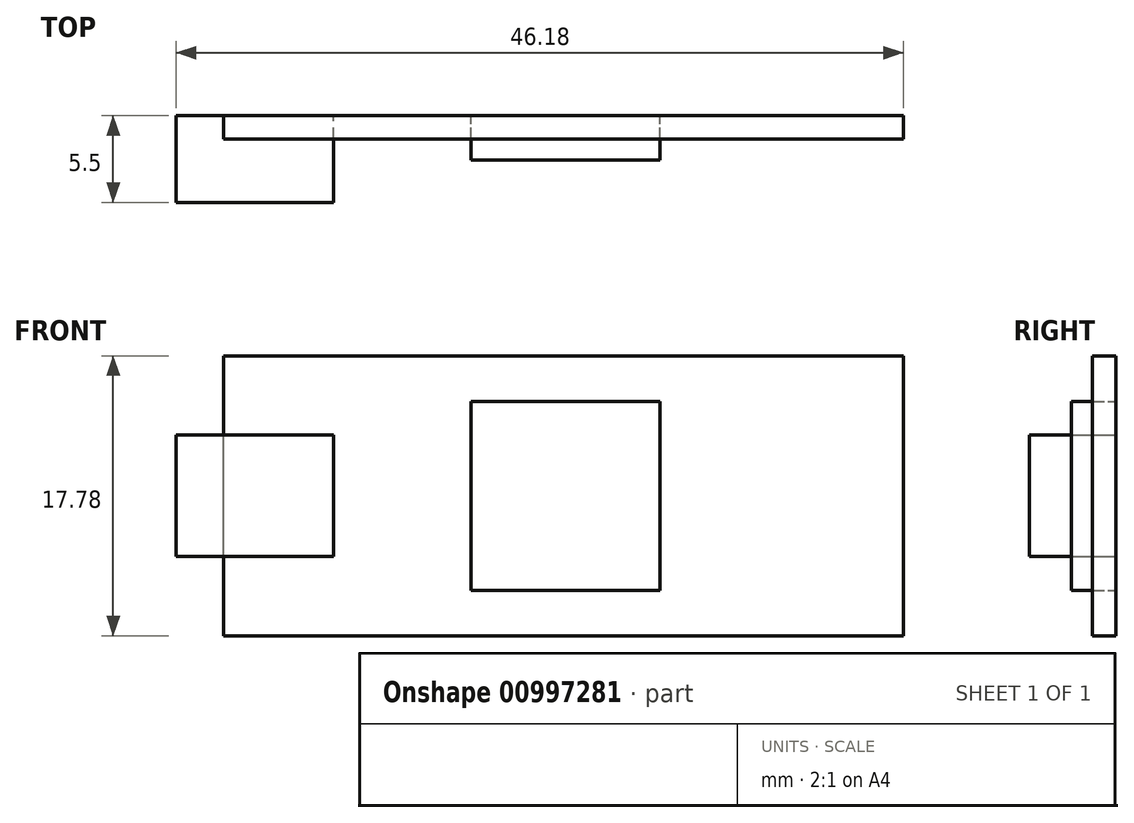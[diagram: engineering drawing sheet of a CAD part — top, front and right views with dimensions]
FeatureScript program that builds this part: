
annotation { "Feature Type Name" : "Feature", "Feature Type Description" : "" }
export const myFeature = defineFeature(function(context is Context, id is Id, definition is map)
    precondition{}
    {
        {
            var Q0;
            Q0=qCreatedBy(makeId("Front.planeOp"),FACE);
            var sketch = newSketch(context, id + "F0", { "sketchPlane" : qUnion([Q0])});
            skLineSegment(sketch, "E0.bottom", {"start": v(-43.18, 25.32) * mm, "end": v(0, 25.32) * mm});
            skLineSegment(sketch, "E0.top", {"start": v(-43.18, 43.1) * mm, "end": v(0, 43.1) * mm});
            skLineSegment(sketch, "E0.left", {"start": v(-43.18, 25.32) * mm, "end": v(-43.18, 43.1) * mm});
            skLineSegment(sketch, "E0.right", {"start": v(0, 25.32) * mm, "end": v(0, 43.1) * mm});
            skSolve(sketch);
        }
        {
            var Q0;
            Q0=qCreatedBy(makeId("Front.planeOp"),FACE);
            var sketch = newSketch(context, id + "F1", { "sketchPlane" : qUnion([Q0])});
            skLineSegment(sketch, "E1.bottom", {"start": v(-27.45, 28.21) * mm, "end": v(-15.45, 28.21) * mm});
            skLineSegment(sketch, "E1.top", {"start": v(-27.45, 40.21) * mm, "end": v(-15.45, 40.21) * mm});
            skLineSegment(sketch, "E1.left", {"start": v(-27.45, 28.21) * mm, "end": v(-27.45, 40.21) * mm});
            skLineSegment(sketch, "E1.right", {"start": v(-15.45, 28.21) * mm, "end": v(-15.45, 40.21) * mm});
            skPoint(sketch, "E2", {"position": v(-27.45, 34.21) * mm});
            skSolve(sketch);
        }
        {
            var Q0;
            Q0=qCreatedBy(makeId("Front.planeOp"),FACE);
            var sketch = newSketch(context, id + "F2", { "sketchPlane" : qUnion([Q0])});
            skLineSegment(sketch, "E3.bottom", {"start": v(-46.18, 38.06) * mm, "end": v(-36.18, 38.06) * mm});
            skLineSegment(sketch, "E3.top", {"start": v(-46.18, 30.36) * mm, "end": v(-36.18, 30.36) * mm});
            skLineSegment(sketch, "E3.left", {"start": v(-46.18, 38.06) * mm, "end": v(-46.18, 30.36) * mm});
            skLineSegment(sketch, "E3.right", {"start": v(-36.18, 38.06) * mm, "end": v(-36.18, 30.36) * mm});
            skPoint(sketch, "E4", {"position": v(-46.18, 34.21) * mm});
            skSolve(sketch);
        }
        {
            var Q0;
            Q0=makeQuery(id+"F0.imprint","IMPRINT",FACE,{"disambiguationData":[TD([[makeQuery(id+"F0.imprint","IMPRINT",EDGE,{"derivedFrom":sQuery(id+"F0.wireOp",EDGE,"E0.bottom")}),1.0]])]});
            extrude(context, id + "F3", {"entities" : qUnion([Q0]), "depth" : 1.5 * mm, "offsetDistance" : 25 * mm});
        }
        {
            var Q0;
            Q0 = qSketchRegion(id + "F1", true);
            extrude(context, id + "F4", {"entities" : qUnion([Q0]), "depth" : 2.82 * mm, "offsetDistance" : 25 * mm});
        }
        {
            var Q0;
            Q0 = qSketchRegion(id + "F2", true);
            extrude(context, id + "F5", {"entities" : qUnion([Q0]), "depth" : 5.5 * mm, "offsetDistance" : 25 * mm});
        }
    });
